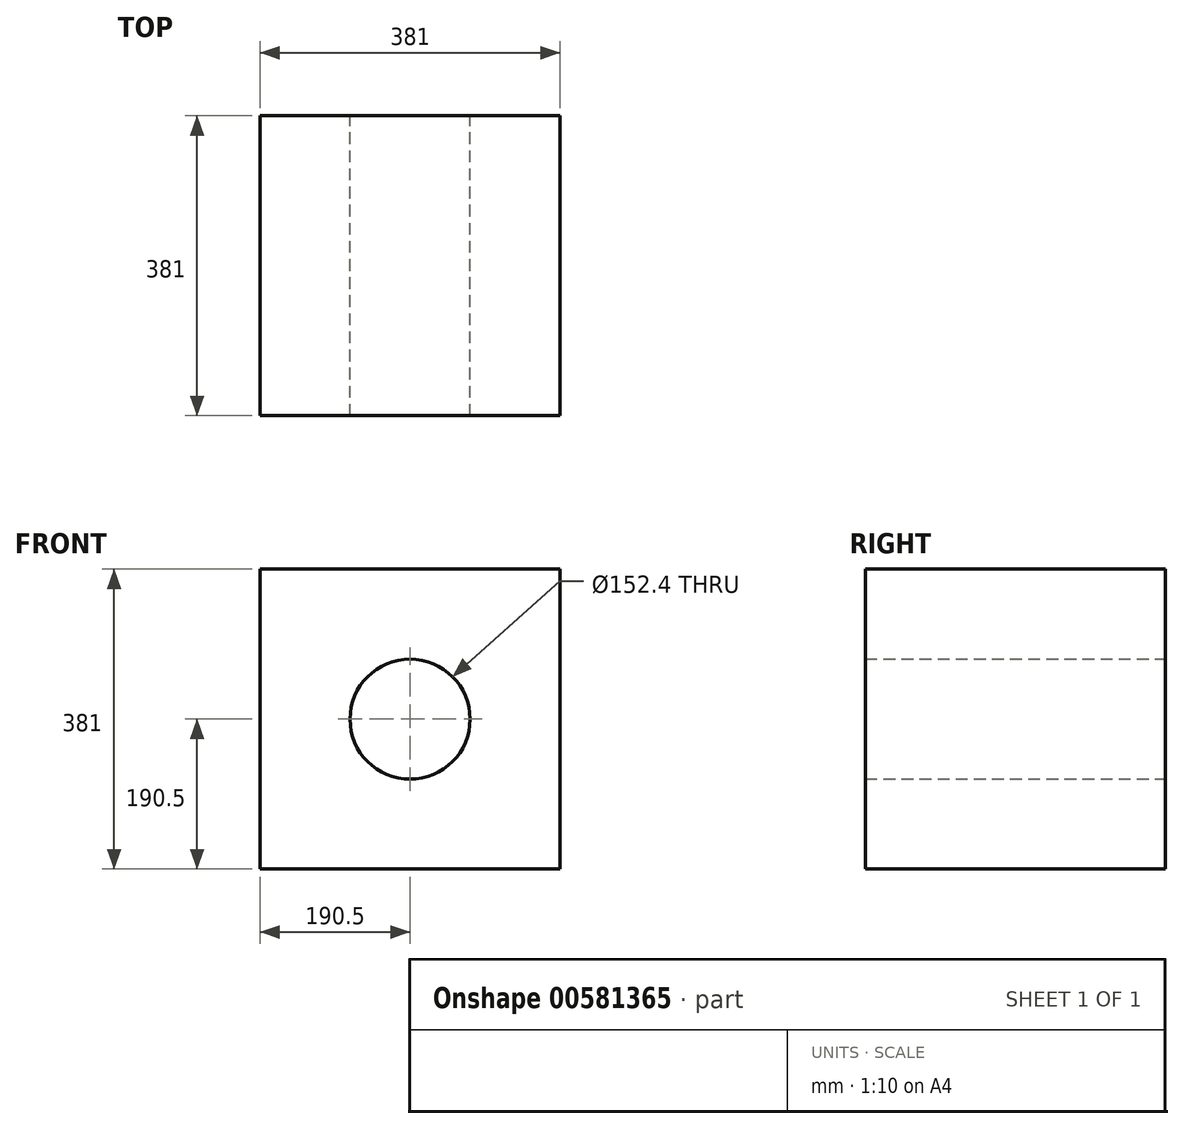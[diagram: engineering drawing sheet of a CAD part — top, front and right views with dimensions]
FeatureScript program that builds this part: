
annotation { "Feature Type Name" : "Feature", "Feature Type Description" : "" }
export const myFeature = defineFeature(function(context is Context, id is Id, definition is map)
    precondition{}
    {
        {
            var Q0;
            Q0=qCreatedBy(makeId("Front.planeOp"),FACE);
            var sketch = newSketch(context, id + "F0", { "sketchPlane" : qUnion([Q0])});
            skLineSegment(sketch, "E0", {"start": v(0, 0) * mm, "end": v(381, 0) * mm});
            skLineSegment(sketch, "E1", {"start": v(381, 0) * mm, "end": v(381, 381) * mm});
            skLineSegment(sketch, "E2", {"start": v(381, 381) * mm, "end": v(0, 381) * mm});
            skLineSegment(sketch, "E3", {"start": v(0, 381) * mm, "end": v(0, 0) * mm});
            skSolve(sketch);
        }
        {
            var Q0;
            Q0=makeQuery(id+"F0.imprint","IMPRINT",FACE,{"disambiguationData":[TD([[makeQuery(id+"F0.imprint","IMPRINT",EDGE,{"derivedFrom":sQuery(id+"F0.wireOp",EDGE,"E0")}),1.0]])]});
            extrude(context, id + "F1", {"entities" : qUnion([Q0]), "depth" : 381 * mm, "offsetDistance" : 25.4 * mm});
        }
        {
            var Q0;
            Q0=makeQuery(id+"F1.opExtrude","CAP_FACE",FACE,{"disambiguationData":[OSD([sQuery(id+"F0.wireOp",EDGE,"E0"),sQuery(id+"F0.wireOp",EDGE,"E1"),sQuery(id+"F0.wireOp",EDGE,"E2"),sQuery(id+"F0.wireOp",EDGE,"E3")])],"isStart":true});
            var sketch = newSketch(context, id + "F2", { "sketchPlane" : qUnion([Q0])});
            skCircle(sketch, "E4", {"center": v(-190.5, 190.5) * mm, "radius": 76.2 * mm});
            skSolve(sketch);
        }
        {
            var Q0;
            Q0=makeQuery(id+"F2.imprint","IMPRINT",FACE,{"disambiguationData":[TD([[makeQuery(id+"F2.imprint","IMPRINT",EDGE,{"derivedFrom":sQuery(id+"F2.wireOp",EDGE,"E4")}),1.0]])]});
            extrude(context, id + "F3", {"entities" : qUnion([Q0]), "operationType" : NewBodyOperationType.REMOVE, "oppositeDirection" : true, "depth" : 381 * mm, "offsetDistance" : 25.4 * mm});
        }
    });
